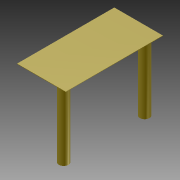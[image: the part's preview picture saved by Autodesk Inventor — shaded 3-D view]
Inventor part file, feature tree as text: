
AUTODESK INVENTOR PART (.ipt)
format: ipt  version: 2011 SP1 (Build 150282100, 282)  size: 90,112 bytes
history: native  units: in
note: dims shown in document units (in); Inventor stores cm internally (conversion verified against a paired STEP export)
features: other x14, extrude x2, sketch x2, pattern_linear x1
ambient origin geometry x8: Origin, YZ Plane, XZ Plane, XY Plane, X Axis, Y Axis, Z Axis, Center Point
bodies: Solid1 (feature_tree)
feature tree (19):
  extrude  "Extrusion1"  Depth=0.172in TaperAngle=0.0deg
  extrude  "Extrusion2"  [1 undecoded]
  pattern_linear  "Rectangular Pattern1"  [2 undecoded]
  other  "to_body_XY"
  other  "to_body_YZ"
  other  "to_body_ZX"
  other  "to_body_X"
  other  "to_body_Y"
  other  "to_body_Z"
  other  "to_body_Center"
  other  "to_body1_XY"
  other  "to_body1_YZ"
  other  "to_body1_ZX"
  other  "to_body1_X"
  other  "to_body1_Y"
  other  "to_body1_Z"
  other  "to_body1_Center"
  sketch  "Sketch_1"  dims[d0=0.001in d1=0.0in d2=0.172in d3=0.0in]
  sketch  "Sketch_2"  dims[d4=0.7874in d6=0.2in d7=0.3937in d9=0.0in]
note: 3 required parameter values undecoded (feature->parameter linkage not recoverable at this tier; creation-order binding heuristic only, values carry confidence <= 0.55)
